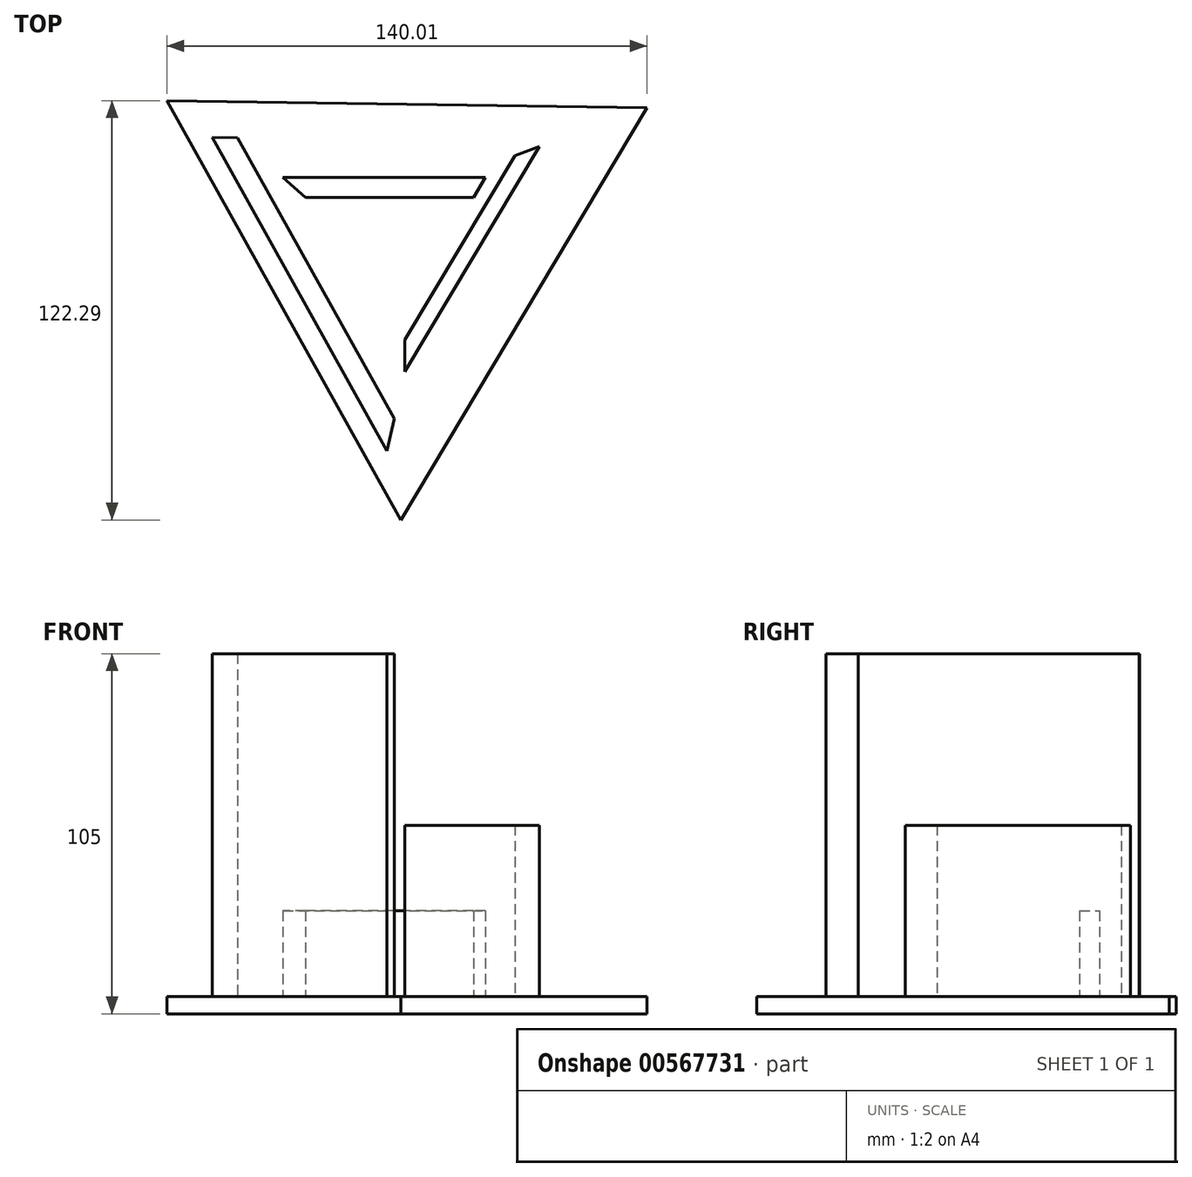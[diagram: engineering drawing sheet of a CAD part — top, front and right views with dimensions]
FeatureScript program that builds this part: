
annotation { "Feature Type Name" : "Feature", "Feature Type Description" : "" }
export const myFeature = defineFeature(function(context is Context, id is Id, definition is map)
    precondition{}
    {
        {
            var Q0;
            Q0=qCreatedBy(makeId("Top.planeOp"),FACE);
            var sketch = newSketch(context, id + "F0", { "sketchPlane" : qUnion([Q0])});
            skCircle(sketch, "E0.cCircle", {"center": v(0, 20.73) * mm, "radius": 40.42 * mm, "construction": true});
            skLineSegment(sketch, "E0.0", {"start": v(70.6, 60.1) * mm, "end": v(-1.2, -60.1) * mm});
            skLineSegment(sketch, "E0.1", {"start": v(-1.2, -60.1) * mm, "end": v(-69.4, 62.18) * mm});
            skLineSegment(sketch, "E0.2", {"start": v(-69.4, 62.18) * mm, "end": v(70.6, 60.1) * mm});
            skPoint(sketch, "E0.0.midPoint", {"position": v(34.7, 0) * mm});
            skSolve(sketch);
        }
        {
            var Q0;
            Q0 = qSketchRegion(id + "F0", true);
            extrude(context, id + "F1", {"entities" : qUnion([Q0]), "depth" : 5 * mm, "offsetDistance" : 25 * mm});
        }
        {
            var Q0;
            Q0=makeQuery(id+"F1.opExtrude","CAP_FACE",FACE,{"disambiguationData":[OSD([sQuery(id+"F0.wireOp",EDGE,"E0.0"),sQuery(id+"F0.wireOp",EDGE,"E0.1"),sQuery(id+"F0.wireOp",EDGE,"E0.2")])],"isStart":false});
            var sketch = newSketch(context, id + "F2", { "sketchPlane" : qUnion([Q0])});
            skLineSegment(sketch, "E1", {"start": v(-56.22, 51.47) * mm, "end": v(-5.24, -39.91) * mm});
            skLineSegment(sketch, "E2", {"start": v(-56.22, 51.47) * mm, "end": v(-48.85, 51.36) * mm});
            skLineSegment(sketch, "E3", {"start": v(-48.85, 51.36) * mm, "end": v(-3.14, -30.58) * mm});
            skLineSegment(sketch, "E4", {"start": v(-3.14, -30.58) * mm, "end": v(-5.24, -39.91) * mm});
            skLineSegment(sketch, "E5", {"start": v(0, -16.84) * mm, "end": v(39.2, 48.8) * mm});
            skLineSegment(sketch, "E6", {"start": v(0, -16.84) * mm, "end": v(0, -7.6) * mm});
            skLineSegment(sketch, "E7", {"start": v(0, -7.6) * mm, "end": v(32.1, 46.16) * mm});
            skLineSegment(sketch, "E8", {"start": v(32.1, 46.16) * mm, "end": v(39.2, 48.8) * mm});
            skLineSegment(sketch, "E9", {"start": v(-35.58, 39.85) * mm, "end": v(23.48, 39.85) * mm});
            skLineSegment(sketch, "E10", {"start": v(23.48, 39.85) * mm, "end": v(19.98, 33.99) * mm});
            skLineSegment(sketch, "E11", {"start": v(19.98, 33.99) * mm, "end": v(-28.94, 33.99) * mm});
            skLineSegment(sketch, "E12", {"start": v(-28.94, 33.99) * mm, "end": v(-35.58, 39.85) * mm});
            skSolve(sketch);
        }
        {
            var Q0;
            Q0=makeQuery(id+"F2.imprint","IMPRINT",FACE,{"disambiguationData":[TD([[makeQuery(id+"F2.imprint","IMPRINT",EDGE,{"derivedFrom":sQuery(id+"F2.wireOp",EDGE,"E1")}),1.0]])]});
            extrude(context, id + "F3", {"entities" : qUnion([Q0]), "operationType" : NewBodyOperationType.ADD, "depth" : 100 * mm, "offsetDistance" : 25 * mm});
        }
        {
            var Q0;
            Q0=makeQuery(id+"F2.imprint","IMPRINT",FACE,{"disambiguationData":[TD([[makeQuery(id+"F2.imprint","IMPRINT",EDGE,{"derivedFrom":sQuery(id+"F2.wireOp",EDGE,"E5")}),1.0]])]});
            extrude(context, id + "F4", {"entities" : qUnion([Q0]), "operationType" : NewBodyOperationType.ADD, "depth" : 50 * mm, "offsetDistance" : 25 * mm});
        }
        {
            var Q0;
            Q0=makeQuery(id+"F2.imprint","IMPRINT",FACE,{"disambiguationData":[TD([[makeQuery(id+"F2.imprint","IMPRINT",EDGE,{"derivedFrom":sQuery(id+"F2.wireOp",EDGE,"E9")}),-1.0]])]});
            extrude(context, id + "F5", {"entities" : qUnion([Q0]), "operationType" : NewBodyOperationType.ADD, "depth" : 25 * mm, "offsetDistance" : 25 * mm});
        }
    });
